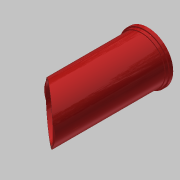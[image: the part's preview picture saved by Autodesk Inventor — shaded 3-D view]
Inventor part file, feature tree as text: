
AUTODESK INVENTOR PART (.ipt)
format: ipt  version: 2017.3 (Build 213257000, 257)  size: 155,136 bytes
history: native  units: in
note: dims shown in document units (in); Inventor stores cm internally (conversion verified against a paired STEP export)
features: extrude x5, sketch x5, fillet x2, chamfer x1
ambient origin geometry x8: Origin, YZ Plane, XZ Plane, XY Plane, X Axis, Y Axis, Z Axis, Center Point
bodies: Solid1 (feature_tree)
feature tree (13):
  extrude  "Extrusion1"  Depth=2.0in TaperAngle=0.0deg
  extrude  "Extrusion2"  Depth=3.75in TaperAngle=0.0deg
  extrude  "Extrusion3"  Depth=68.7402in TaperAngle=0.0deg
  extrude  "Extrusion4"  Depth=0.0312in TaperAngle=0.0deg
  chamfer  "Chamfer1"  Distance=0.0312in Angle=45.0deg
  fillet  "Fillet1"  Radius=0.0312in
  fillet  "Fillet2"  Radius=0.0312in
  extrude  "Extrusion5"  Depth=1.0in TaperAngle=0.0deg
  sketch  "Sketch1"  dims[d0=30.02in d1=2.0in d2=0.0in]
  sketch  "Sketch2"  dims[d3=28.52in d4=3.75in d5=0.0in]
  sketch  "Sketch3"  dims[d6=27.5in d7=68.7402in d8=0.0in]
  sketch  "Sketch4"  dims[d9=25.0in d11=30.9055in d12=0.0in d13=0.0312in d14=0.125in d15=45.0deg d16=0.0312in d17=0.0312in]
  sketch  "Sketch5"  dims[d18=0.2749in d19=1.0in d20=0.0in d24=0.25in]
